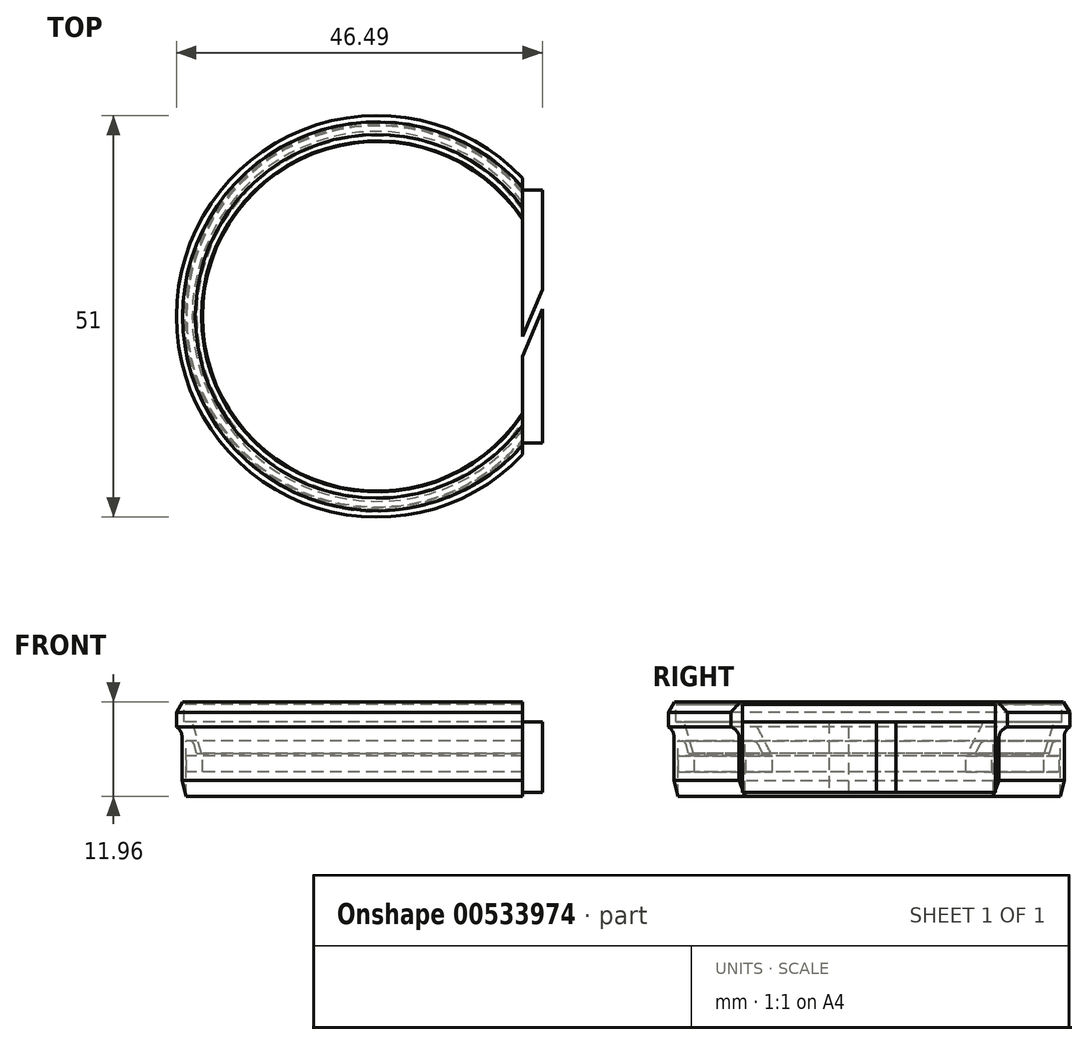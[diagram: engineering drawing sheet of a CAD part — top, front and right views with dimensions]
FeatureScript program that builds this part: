
annotation { "Feature Type Name" : "Feature", "Feature Type Description" : "" }
export const myFeature = defineFeature(function(context is Context, id is Id, definition is map)
    precondition{}
    {
        {
            var Q0;
            Q0=qCreatedBy(makeId("Front.planeOp"),FACE);
            var sketch = newSketch(context, id + "F0", { "sketchPlane" : qUnion([Q0])});
            skLineSegment(sketch, "E0", {"start": v(-25.5, 0) * mm, "end": v(-25.5, -3.16) * mm});
            skLineSegment(sketch, "E1", {"start": v(-25.5, -3.16) * mm, "end": v(-24.8, -3.16) * mm});
            skLineSegment(sketch, "E2", {"start": v(-24.8, -3.16) * mm, "end": v(-24.8, -11.96) * mm});
            skLineSegment(sketch, "E3", {"start": v(-24.8, -11.96) * mm, "end": v(-24.3, -11.96) * mm});
            skLineSegment(sketch, "E4", {"start": v(-24.3, -11.96) * mm, "end": v(-24.3, -4.96) * mm});
            skLineSegment(sketch, "E5", {"start": v(-24.3, -4.96) * mm, "end": v(-23.4, -4.96) * mm});
            skLineSegment(sketch, "E6", {"start": v(-23.4, -4.96) * mm, "end": v(-22.93, -6.5) * mm});
            skLineSegment(sketch, "E7", {"start": v(-22.93, -6.5) * mm, "end": v(-22.3, -6.5) * mm});
            skLineSegment(sketch, "E8", {"start": v(-22.3, -6.5) * mm, "end": v(-23.5, -2.5) * mm});
            skLineSegment(sketch, "E9", {"start": v(-23.5, -2.5) * mm, "end": v(-24.5, -2.5) * mm});
            skLineSegment(sketch, "E10", {"start": v(-24.5, -2.5) * mm, "end": v(-24.5, 0) * mm});
            skLineSegment(sketch, "E11", {"start": v(-24.5, 0) * mm, "end": v(-25.5, 0) * mm});
            skLineSegment(sketch, "E12", {"start": v(0, 17.82) * mm, "end": v(0, -15.68) * mm});
            skLineSegment(sketch, "E13", {"start": v(-24.5, 0) * mm, "end": v(-23.1, 0) * mm});
            skLineSegment(sketch, "E14", {"start": v(-23.1, 0) * mm, "end": v(-23.1, -0.3) * mm});
            skLineSegment(sketch, "E15", {"start": v(-23.1, -0.3) * mm, "end": v(-24.5, -0.3) * mm});
            skLineSegment(sketch, "E16.bottom", {"start": v(-24.2, -6.86) * mm, "end": v(-22.2, -6.86) * mm});
            skLineSegment(sketch, "E16.top", {"start": v(-24.2, -8.86) * mm, "end": v(-22.2, -8.86) * mm});
            skLineSegment(sketch, "E16.left", {"start": v(-24.2, -6.86) * mm, "end": v(-24.2, -8.86) * mm});
            skLineSegment(sketch, "E16.right", {"start": v(-22.2, -6.86) * mm, "end": v(-22.2, -8.86) * mm});
            skSolve(sketch);
        }
        {
            var Q0;
            Q0=qSketchRegion(id+"F0",true);
            var Q1;
            Q1=sQuery(id+"F0.wireOp",EDGE,"E12");
            revolve(context, id + "F1", {"entities" : qUnion([Q0]), "axis" : qUnion([Q1]), "revolveType" : RevolveType.FULL});
        }
        {
            var Q0;
            Q0=makeQuery(id+"F1.opRevolve","SWEPT_EDGE",EDGE,{"disambiguationData":[OSD([sQuery(id+"F0.wireOp",EDGE,"E0"),sQuery(id+"F0.wireOp",EDGE,"E11")])]});
            chamfer(context, id + "F2", {"entities" : qUnion([Q0]), "chamferType" : ChamferType.TWO_OFFSETS, "width1" : .8 * mm, "oppositeDirection" : false, "width2" : 1.3 * mm, "tangentPropagation" : true});
        }
        {
            var Q0;
            Q0=makeQuery(id+"F1.opRevolve","SWEPT_EDGE",EDGE,{"disambiguationData":[OSD([sQuery(id+"F0.wireOp",EDGE,"E1"),sQuery(id+"F0.wireOp",EDGE,"E2")])]});
            fillet(context, id + "F3", {"entities" : qUnion([Q0]), "radius" : 1.4 * mm, "tangentPropagation" : true, "allowEdgeOverflow" : false});
        }
        {
            var Q0;
            Q0=makeQuery(id+"F1.opRevolve","SWEPT_EDGE",EDGE,{"disambiguationData":[OSD([sQuery(id+"F0.wireOp",EDGE,"E2"),sQuery(id+"F0.wireOp",EDGE,"E3")])]});
            chamfer(context, id + "F4", {"entities" : qUnion([Q0]), "chamferType" : ChamferType.TWO_OFFSETS, "width1" : 2 * mm, "oppositeDirection" : false, "width2" : .5 * mm, "tangentPropagation" : true});
        }
        {
            var Q0;
            Q0=makeQuery(id+"F1.opRevolve","SWEPT_EDGE",EDGE,{"disambiguationData":[OSD([sQuery(id+"F0.wireOp",EDGE,"E5"),sQuery(id+"F0.wireOp",EDGE,"E6")])]});
            fillet(context, id + "F5", {"entities" : qUnion([Q0]), "radius" : .5 * mm, "tangentPropagation" : true, "allowEdgeOverflow" : false});
        }
        {
            var Q0;
            Q0=qCreatedBy(makeId("Top.planeOp"),FACE);
            var sketch = newSketch(context, id + "F6", { "sketchPlane" : qUnion([Q0])});
            skLineSegment(sketch, "E17", {"start": v(18.5, 14.5) * mm, "end": v(18.5, -14.5) * mm});
            skLineSegment(sketch, "E18.bottom", {"start": v(18.5, 29.3) * mm, "end": v(60.37, 29.3) * mm});
            skLineSegment(sketch, "E18.top", {"start": v(18.5, -27.33) * mm, "end": v(60.37, -27.33) * mm});
            skLineSegment(sketch, "E18.left", {"start": v(18.5, 29.3) * mm, "end": v(18.5, -27.33) * mm});
            skLineSegment(sketch, "E18.right", {"start": v(60.37, 29.3) * mm, "end": v(60.37, -27.33) * mm});
            skLineSegment(sketch, "E19", {"start": v(18.5, 17.56) * mm, "end": v(23.5, 17.56) * mm});
            skLineSegment(sketch, "E20", {"start": v(23.5, 17.56) * mm, "end": v(23.5, -17.56) * mm});
            skLineSegment(sketch, "E21", {"start": v(18.5, -17.56) * mm, "end": v(23.5, -17.56) * mm});
            skSolve(sketch);
        }
        {
            var Q0;
            Q0 = qSketchRegion(id + "F6", true);
            extrude(context, id + "F7", {"entities" : qUnion([Q0]), "operationType" : NewBodyOperationType.REMOVE, "oppositeDirection" : true, "depth" : 25 * mm, "offsetDistance" : 25 * mm});
        }
        {
            var Q0;
            Q0=makeQuery(id+"F1.opRevolve","SWEPT_FACE",FACE,{"disambiguationData":[OSD([sQuery(id+"F0.wireOp",EDGE,"E9")])]});
            var sketch = newSketch(context, id + "F8", { "sketchPlane" : qUnion([Q0])});
            skLineSegment(sketch, "E22", {"start": v(18.5, 16.07) * mm, "end": v(21, 16.07) * mm});
            skLineSegment(sketch, "E23", {"start": v(21, 16.07) * mm, "end": v(21, -16.07) * mm});
            skLineSegment(sketch, "E24", {"start": v(18.5, -16.07) * mm, "end": v(21, -16.07) * mm});
            skLineSegment(sketch, "E25", {"start": v(18.5, 16.07) * mm, "end": v(18.5, -16.07) * mm});
            skSolve(sketch);
        }
        {
            var Q0;
            {var subQ4=sQuery(id+"F8.wireOp",EDGE,"E22");Q0=makeQuery(id+"F8.imprint","IMPRINT",FACE,{"disambiguationData":[TD([[makeQuery(id+"F8.imprint","IMPRINT",EDGE,{"derivedFrom":subQ4}),-1.0]])]});}
            extrude(context, id + "F9", {"entities" : qUnion([Q0]), "operationType" : NewBodyOperationType.ADD, "oppositeDirection" : true, "depth" : 9 * mm, "offsetDistance" : 25 * mm});
        }
        {
            var Q0;
            Q0=qCreatedBy(makeId("Top.planeOp"),FACE);
            var sketch = newSketch(context, id + "F10", { "sketchPlane" : qUnion([Q0])});
            skLineSegment(sketch, "E26", {"start": v(16, -8.57) * mm, "end": v(28.5, 21.43) * mm});
            skLineSegment(sketch, "E27", {"start": v(28.5, 18.93) * mm, "end": v(28.5, 21.43) * mm});
            skLineSegment(sketch, "E28", {"start": v(28.5, 18.93) * mm, "end": v(16, -11.07) * mm});
            skLineSegment(sketch, "E29", {"start": v(16, -11.07) * mm, "end": v(16, -8.57) * mm});
            skSolve(sketch);
        }
        {
            var Q0;
            Q0 = qSketchRegion(id + "F10", true);
            extrude(context, id + "F11", {"entities" : qUnion([Q0]), "operationType" : NewBodyOperationType.REMOVE, "oppositeDirection" : true, "depth" : 100 * mm, "offsetDistance" : 25 * mm});
        }
    });
